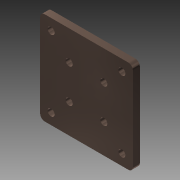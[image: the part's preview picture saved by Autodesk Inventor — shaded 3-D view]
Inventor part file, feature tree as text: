
AUTODESK INVENTOR PART (.ipt)
format: ipt  version: 2015 (Build 190159000, 159)  size: 116,736 bytes
history: native  units: mm
features: extrude x1, fillet x1, sketch x1
ambient origin geometry x8: Origin, YZ Plane, XZ Plane, XY Plane, X Axis, Y Axis, Z Axis, Center Point
bodies: Body1 (feature_tree)
feature tree (3):
  extrude  "Extrusion3"  Depth=36.0mm
  fillet  "Fillet2"  Radius=40.0mm
  sketch  "Sketch1"  dims[d0=36.0mm d1=36.0mm d50=40.0mm d51=40.0mm d55=3.0mm d56=3.0mm d57=3.0mm d58=3.0mm d59=3.0mm d60=0.0mm d61=2.0mm]
